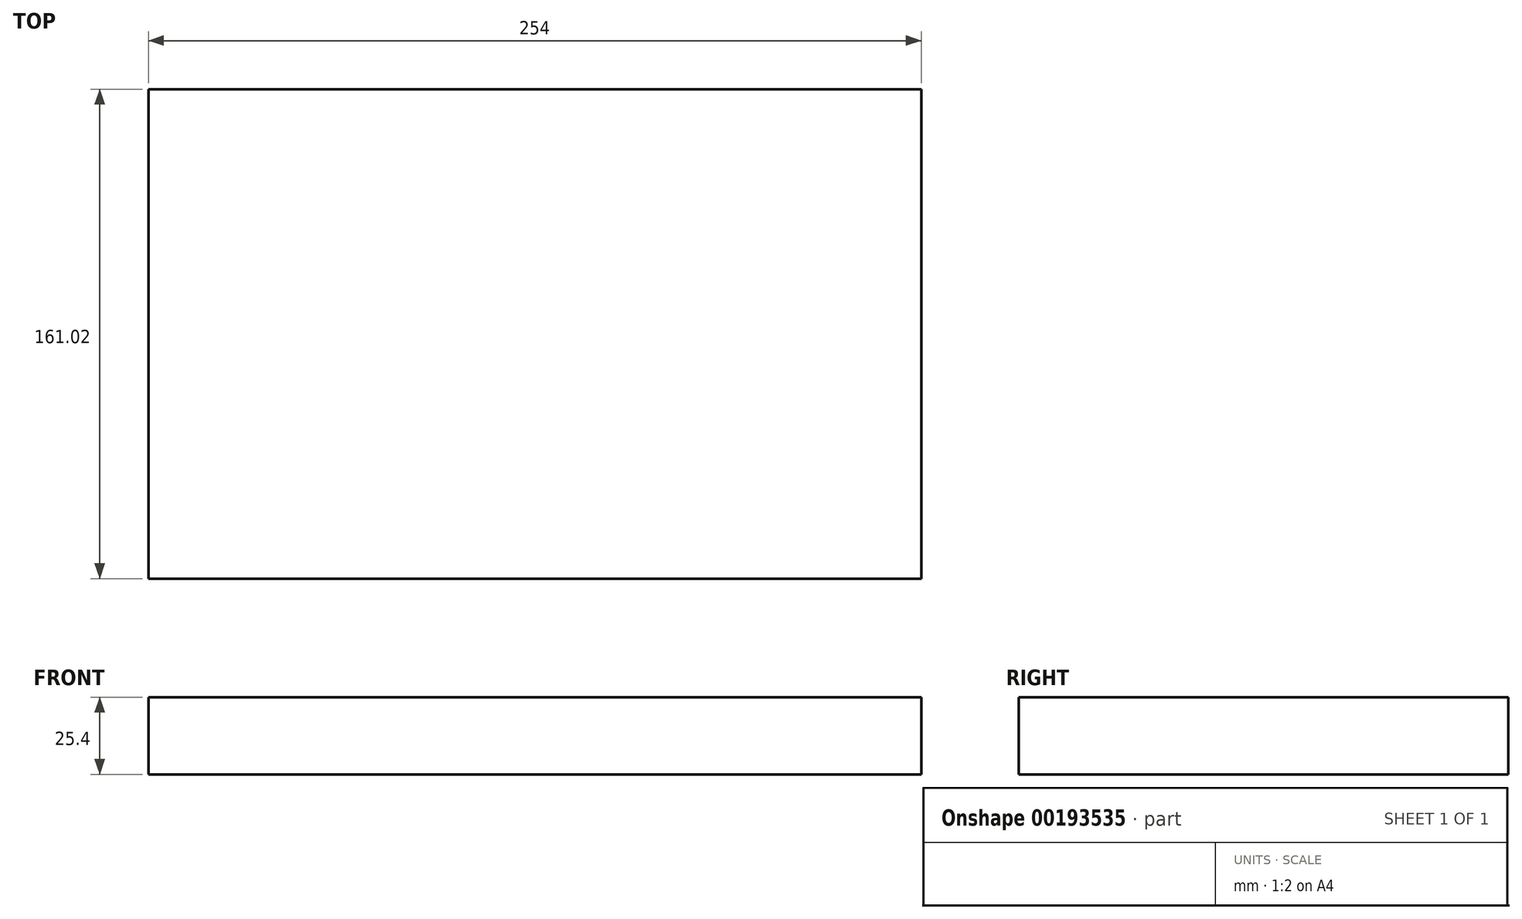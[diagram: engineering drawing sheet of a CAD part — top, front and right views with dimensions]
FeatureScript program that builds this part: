
annotation { "Feature Type Name" : "Feature", "Feature Type Description" : "" }
export const myFeature = defineFeature(function(context is Context, id is Id, definition is map)
    precondition{}
    {
        {
            var Q0;
            Q0=qCreatedBy(makeId("Top.planeOp"),FACE);
            var sketch = newSketch(context, id + "F0", { "sketchPlane" : qUnion([Q0])});
            skLineSegment(sketch, "E0.bottom", {"start": v(-127, 80.5) * mm, "end": v(127, 80.5) * mm});
            skLineSegment(sketch, "E0.top", {"start": v(-127, -80.5) * mm, "end": v(127, -80.5) * mm});
            skLineSegment(sketch, "E0.left", {"start": v(-127, 80.5) * mm, "end": v(-127, -80.5) * mm});
            skLineSegment(sketch, "E0.right", {"start": v(127, 80.5) * mm, "end": v(127, -80.5) * mm});
            skPoint(sketch, "E0.middle", {"position": v(0, 0) * mm});
            skLineSegment(sketch, "E1", {"start": v(0, 58.7) * mm, "end": v(19.11, 58.7) * mm});
            skLineSegment(sketch, "E2", {"start": v(19.11, 58.7) * mm, "end": v(19.11, 41.41) * mm});
            skLineSegment(sketch, "E3", {"start": v(19.11, 41.41) * mm, "end": v(58.25, 28.37) * mm});
            skLineSegment(sketch, "E4", {"start": v(58.25, 28.37) * mm, "end": v(61.29, 0) * mm});
            skLineSegment(sketch, "E5", {"start": v(61.29, 0.15) * mm, "end": v(14.56, -33.53) * mm});
            skLineSegment(sketch, "E6", {"start": v(14.56, -33.53) * mm, "end": v(0, -36.56) * mm});
            skSolve(sketch);
        }
        {
            var Q0;
            Q0=makeQuery(id+"F0.imprint","IMPRINT",FACE,{"disambiguationData":[TD([[makeQuery(id+"F0.imprint","IMPRINT",EDGE,{"derivedFrom":sQuery(id+"F0.wireOp",EDGE,"E0.bottom")}),-1.0]])]});
            extrude(context, id + "F1", {"entities" : qUnion([Q0]), "depth" : 25.4 * mm});
        }
    });
